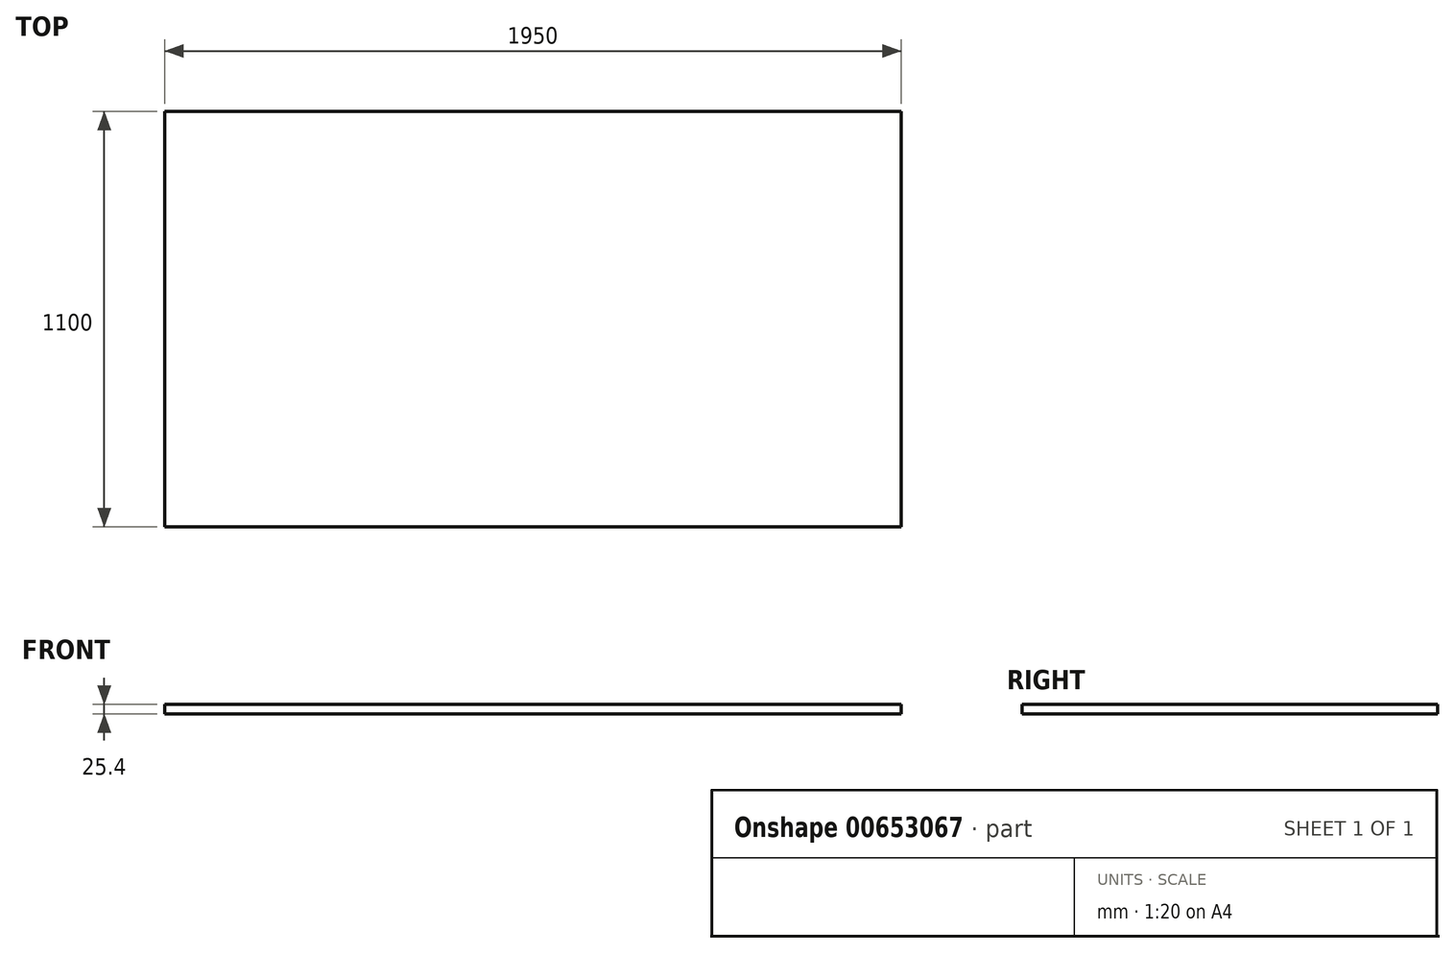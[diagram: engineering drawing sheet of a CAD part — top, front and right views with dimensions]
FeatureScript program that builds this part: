
annotation { "Feature Type Name" : "Feature", "Feature Type Description" : "" }
export const myFeature = defineFeature(function(context is Context, id is Id, definition is map)
    precondition{}
    {
        {
            var Q0;
            Q0=qCreatedBy(makeId("Front.planeOp"),FACE);
            var sketch = newSketch(context, id + "F0", { "sketchPlane" : qUnion([Q0])});
            skLineSegment(sketch, "E0.bottom", {"start": v(975, -12.7) * mm, "end": v(-975, -12.7) * mm});
            skLineSegment(sketch, "E0.top", {"start": v(975, 12.7) * mm, "end": v(-975, 12.7) * mm});
            skLineSegment(sketch, "E0.left", {"start": v(975, -12.7) * mm, "end": v(975, 12.7) * mm});
            skLineSegment(sketch, "E0.right", {"start": v(-975, -12.7) * mm, "end": v(-975, 12.7) * mm});
            skPoint(sketch, "E0.middle", {"position": v(0, 0) * mm});
            skSolve(sketch);
        }
        {
            var Q0;
            Q0 = qSketchRegion(id + "F0", true);
            extrude(context, id + "F1", {"entities" : qUnion([Q0]), "depth" : 1100 * mm, "offsetDistance" : 25 * mm});
        }
    });
